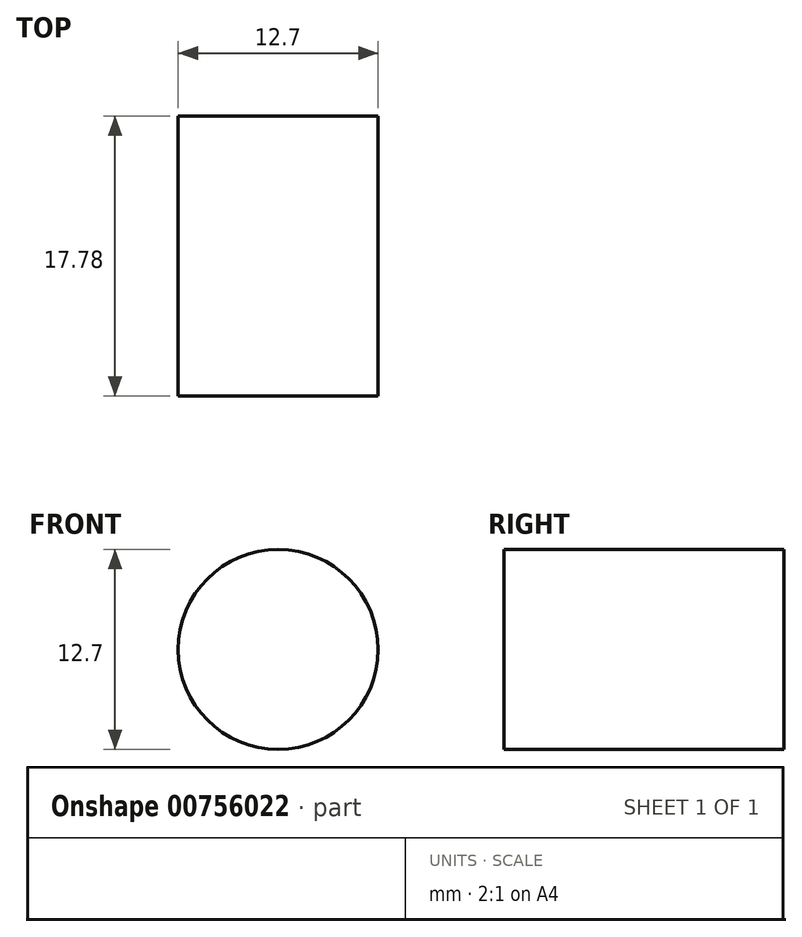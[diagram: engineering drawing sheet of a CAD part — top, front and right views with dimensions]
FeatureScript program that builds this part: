
annotation { "Feature Type Name" : "Feature", "Feature Type Description" : "" }
export const myFeature = defineFeature(function(context is Context, id is Id, definition is map)
    precondition{}
    {
        {
            var Q0;
            Q0=qCreatedBy(makeId("Front.planeOp"),FACE);
            var sketch = newSketch(context, id + "F0", { "sketchPlane" : qUnion([Q0])});
            skCircle(sketch, "E0", {"center": v(0, 0) * mm, "radius": 6.35 * mm});
            skSolve(sketch);
        }
        {
            var Q0;
            Q0=makeQuery(id+"F0.imprint","IMPRINT",FACE,{"disambiguationData":[TD([[makeQuery(id+"F0.imprint","IMPRINT",EDGE,{"derivedFrom":sQuery(id+"F0.wireOp",EDGE,"E0")}),1.0]])]});
            extrude(context, id + "F1", {"entities" : qUnion([Q0]), "depth" : 17.78 * mm, "offsetDistance" : 25.4 * mm});
        }
    });
